# Revit family: Mezcladora de lavabo EP2006-1.9
name_source: partatom
category: Plumbing Fixtures
revit_build: Autodesk Revit 2015 (Build: 20140223_1515(x64)
units: mm (PartAtom-declared; Revit-internal decimal feet)

## types (1)
- EP2006-1.9
    CW Connection = Yes
    Chrome = Brass Chromed
    Default Elevation = 1"
    Description = Ensamble de 8" a 12" con desaguüe de push, con descarga de 1.9 lpm
    HW Connection = Yes
    Inlet Threads = ½" - 14 NPSM
    Manufacturer = HELVEX S.A. de C.V.
    Max. Working Pressure = 85.3 psi
    Min. Working Pressure = 2.9 psi
    Model = EP2006-1.9
    Niquel Duravex = Niquel Duravex
    Satin = Brass Satín
    Total Height = 4"
    Total Length = 7"
    Type Comments = Mezcladora para lavabo con desagüe de push, instalación de 8" a 12" con Valvex V de discos cerámicos de 1/4 de vuelta.
    Type Image = EP2006-1.9.JPG
    URL = http://www.helvex.com.mx

## geometry (parser evidence)
native form markers: Sweep x3
no freeform markers — native parametric forms only
